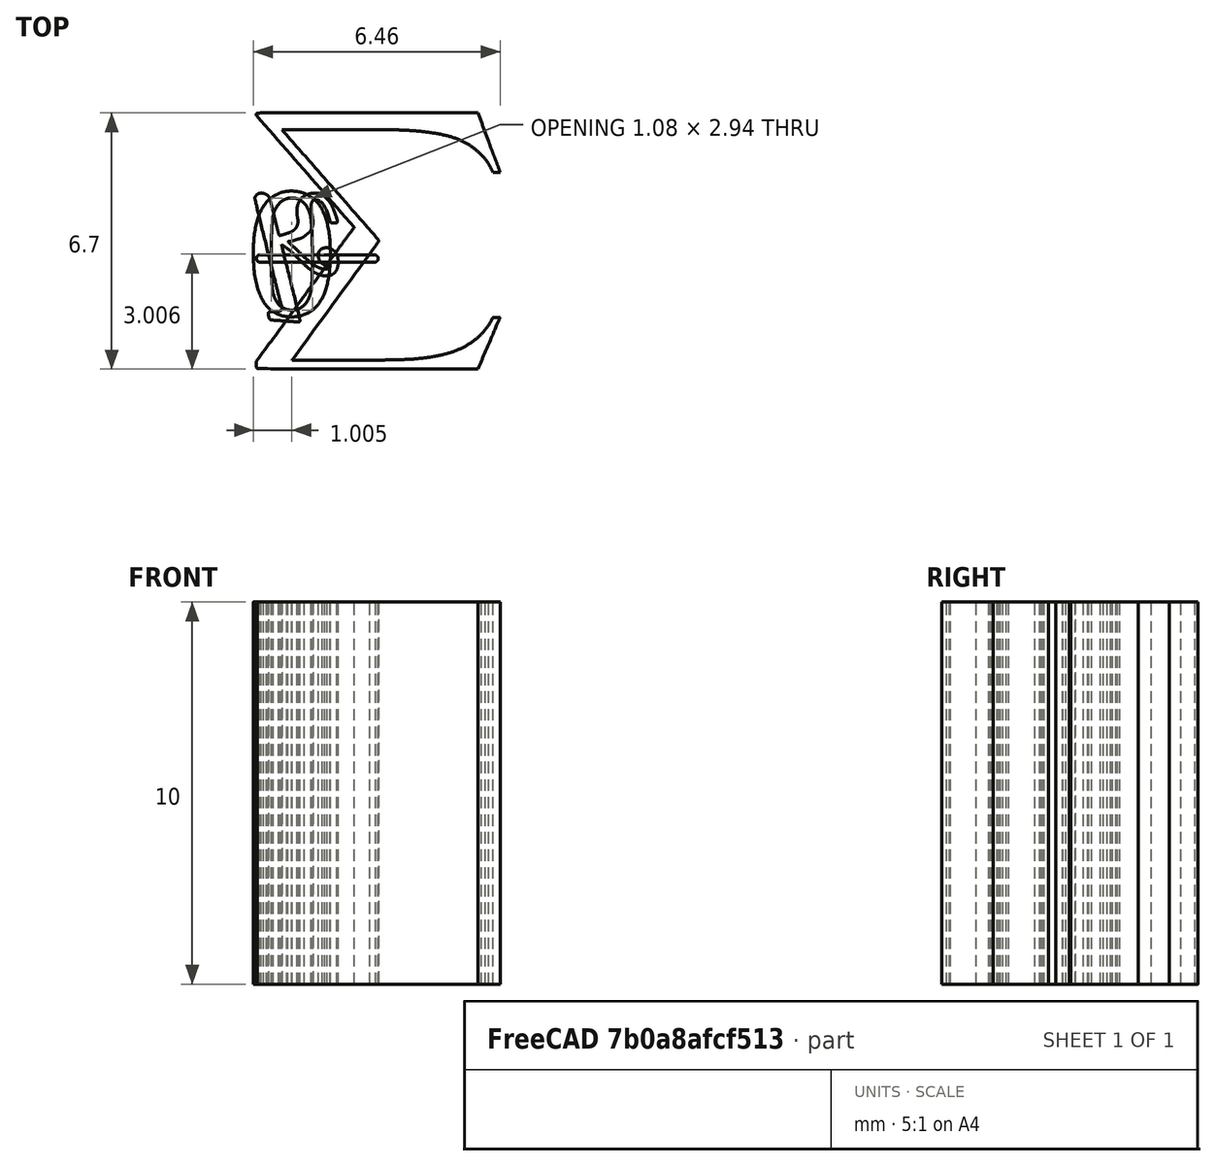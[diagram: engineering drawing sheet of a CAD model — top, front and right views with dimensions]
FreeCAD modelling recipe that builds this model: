
FCSTD DOCUMENT  (FreeCAD 0.19R)
Label: 9
License: All rights reserved
LicenseURL: http://en.wikipedia.org/wiki/All_rights_reserved
objects: Part::Feature×8, Sketcher::SketchObject×4, PartDesign::Pad×4, PartDesign::Body×4
note: 24 computed .brp shape members not serialized (recipe doc carries the construction recipe); baked Part::Feature solids carry a one-line shape summary decoded from their .brp

FEATURE [Part::Feature] MJX_11_TEX_LO_2211
  shape: bbox 6.384 x 6.704 x 2e-07 mm, 0 faces, 0 solids (baked)
FEATURE [Part::Feature] MJX_11_TEX_I_6B
  shape: bbox 2.179 x 3.376 x 2e-07 mm, 0 faces, 0 solids (baked)
FEATURE [Part::Feature] MJX_11_TEX_N_3D
  shape: bbox 3.189 x 0.1916 x 2e-07 mm, 0 faces, 0 solids (baked)
FEATURE [Part::Feature] MJX_11_TEX_N_3D001
  shape: bbox 3.189 x 0.1916 x 2e-07 mm, 0 faces, 0 solids (baked)
FEATURE [Part::Feature] MJX_11_TEX_N_30
  shape: bbox 2.016 x 3.295 x 2e-07 mm, 0 faces, 0 solids (baked)
FEATURE [Part::Feature] MJX_11_TEX_N_30001
  shape: bbox 1.077 x 2.936 x 2e-07 mm, 0 faces, 0 solids (baked)
FEATURE [Part::Feature] MJX_11_TEX_N_32
  shape: bbox 1.911 x 3.189 x 2e-07 mm, 0 faces, 0 solids (baked)
FEATURE [Part::Feature] MJX_11_TEX_N_33
  shape: bbox 1.987 x 3.29 x 2e-07 mm, 0 faces, 0 solids (baked)
FEATURE [Sketcher::SketchObject] Sketch
  FullyConstrained = false
  MapMode = 5
  Support = -> [XY_Plane]
  sketch-geometry (43):
    g0: BSplineCurve PolesCount=3 KnotsCount=2 Degree=2 IsPeriodic=0
    g1: BSplineCurve PolesCount=2 KnotsCount=2 Degree=1 IsPeriodic=0
    g2: BSplineCurve PolesCount=2 KnotsCount=2 Degree=1 IsPeriodic=0
    g3: BSplineCurve PolesCount=3 KnotsCount=2 Degree=2 IsPeriodic=0
    g4: BSplineCurve PolesCount=2 KnotsCount=2 Degree=1 IsPeriodic=0
    g5: BSplineCurve PolesCount=2 KnotsCount=2 Degree=1 IsPeriodic=0
    g6: BSplineCurve PolesCount=3 KnotsCount=2 Degree=2 IsPeriodic=0
    g7: BSplineCurve PolesCount=3 KnotsCount=2 Degree=2 IsPeriodic=0
    g8: BSplineCurve PolesCount=3 KnotsCount=2 Degree=2 IsPeriodic=0
    g9: BSplineCurve PolesCount=3 KnotsCount=2 Degree=2 IsPeriodic=0
    g10: BSplineCurve PolesCount=3 KnotsCount=2 Degree=2 IsPeriodic=0
    g11: BSplineCurve PolesCount=2 KnotsCount=2 Degree=1 IsPeriodic=0
    g12: BSplineCurve PolesCount=2 KnotsCount=2 Degree=1 IsPeriodic=0
    g13: BSplineCurve PolesCount=2 KnotsCount=2 Degree=1 IsPeriodic=0
    g14: BSplineCurve PolesCount=2 KnotsCount=2 Degree=1 IsPeriodic=0
    g15: BSplineCurve PolesCount=3 KnotsCount=2 Degree=2 IsPeriodic=0
    g16: BSplineCurve PolesCount=3 KnotsCount=2 Degree=2 IsPeriodic=0
    g17: BSplineCurve PolesCount=3 KnotsCount=2 Degree=2 IsPeriodic=0
    g18: BSplineCurve PolesCount=2 KnotsCount=2 Degree=1 IsPeriodic=0
    g19: BSplineCurve PolesCount=3 KnotsCount=2 Degree=2 IsPeriodic=0
    g20: BSplineCurve PolesCount=3 KnotsCount=2 Degree=2 IsPeriodic=0
    g21: BSplineCurve PolesCount=3 KnotsCount=2 Degree=2 IsPeriodic=0
    g22: BSplineCurve PolesCount=3 KnotsCount=2 Degree=2 IsPeriodic=0
    g23: BSplineCurve PolesCount=3 KnotsCount=2 Degree=2 IsPeriodic=0
    g24: BSplineCurve PolesCount=3 KnotsCount=2 Degree=2 IsPeriodic=0
    g25: BSplineCurve PolesCount=3 KnotsCount=2 Degree=2 IsPeriodic=0
    g26: BSplineCurve PolesCount=3 KnotsCount=2 Degree=2 IsPeriodic=0
    g27: BSplineCurve PolesCount=2 KnotsCount=2 Degree=1 IsPeriodic=0
    g28: BSplineCurve PolesCount=3 KnotsCount=2 Degree=2 IsPeriodic=0
    g29: BSplineCurve PolesCount=3 KnotsCount=2 Degree=2 IsPeriodic=0
    g30: BSplineCurve PolesCount=3 KnotsCount=2 Degree=2 IsPeriodic=0
    g31: BSplineCurve PolesCount=2 KnotsCount=2 Degree=1 IsPeriodic=0
    g32: BSplineCurve PolesCount=2 KnotsCount=2 Degree=1 IsPeriodic=0
    g33: BSplineCurve PolesCount=3 KnotsCount=2 Degree=2 IsPeriodic=0
    g34: BSplineCurve PolesCount=3 KnotsCount=2 Degree=2 IsPeriodic=0
    g35: BSplineCurve PolesCount=3 KnotsCount=2 Degree=2 IsPeriodic=0
    g36: BSplineCurve PolesCount=2 KnotsCount=2 Degree=1 IsPeriodic=0
    g37: BSplineCurve PolesCount=3 KnotsCount=2 Degree=2 IsPeriodic=0
    g38: BSplineCurve PolesCount=3 KnotsCount=2 Degree=2 IsPeriodic=0
    g39: BSplineCurve PolesCount=3 KnotsCount=2 Degree=2 IsPeriodic=0
    g40: BSplineCurve PolesCount=2 KnotsCount=2 Degree=1 IsPeriodic=0
    g41: BSplineCurve PolesCount=2 KnotsCount=2 Degree=1 IsPeriodic=0
    g42: BSplineCurve PolesCount=3 KnotsCount=2 Degree=2 IsPeriodic=0
  constraints (43):
    c: Coincident(g0,g1)
    c: Coincident(g1,g2)
    c: Coincident(g2,g3)
    c: Coincident(g3,g4)
    c: Coincident(g4,g5)
    c: Coincident(g5,g6)
    c: Coincident(g6,g7)
    c: Coincident(g7,g8)
    c: Coincident(g8,g9)
    c: Coincident(g9,g10)
    c: Coincident(g10,g11)
    c: Coincident(g11,g12)
    c: Coincident(g12,g13)
    c: Coincident(g13,g14)
    c: Coincident(g14,g15)
    c: Coincident(g15,g16)
    c: Coincident(g16,g17)
    c: Coincident(g17,g18)
    c: Coincident(g18,g19)
    c: Coincident(g19,g20)
    c: Coincident(g20,g21)
    c: Coincident(g21,g22)
    c: Coincident(g22,g23)
    c: Coincident(g23,g24)
    c: Coincident(g24,g25)
    c: Coincident(g25,g26)
    c: Coincident(g26,g27)
    c: Coincident(g27,g28)
    c: Coincident(g28,g29)
    c: Coincident(g29,g30)
    c: Coincident(g30,g31)
    c: Coincident(g31,g32)
    c: Coincident(g32,g33)
    c: Coincident(g33,g34)
    c: Coincident(g34,g35)
    c: Coincident(g35,g36)
    c: Coincident(g36,g37)
    c: Coincident(g37,g38)
    c: Coincident(g38,g39)
    c: Coincident(g39,g40)
    c: Coincident(g40,g41)
    c: Coincident(g41,g42)
    c: Coincident(g42,g0)
FEATURE [Sketcher::SketchObject] Sketch001
  FullyConstrained = false
  MapMode = 5
  Support = -> [XY_Plane003]
  sketch-geometry (70):
    g0: BSplineCurve PolesCount=3 KnotsCount=2 Degree=2 IsPeriodic=0
    g1: BSplineCurve PolesCount=3 KnotsCount=2 Degree=2 IsPeriodic=0
    g2: BSplineCurve PolesCount=3 KnotsCount=2 Degree=2 IsPeriodic=0
    g3: BSplineCurve PolesCount=3 KnotsCount=2 Degree=2 IsPeriodic=0
    g4: BSplineCurve PolesCount=3 KnotsCount=2 Degree=2 IsPeriodic=0
    g5: BSplineCurve PolesCount=3 KnotsCount=2 Degree=2 IsPeriodic=0
    g6: BSplineCurve PolesCount=3 KnotsCount=2 Degree=2 IsPeriodic=0
    g7: BSplineCurve PolesCount=3 KnotsCount=2 Degree=2 IsPeriodic=0
    g8: BSplineCurve PolesCount=3 KnotsCount=2 Degree=2 IsPeriodic=0
    g9: BSplineCurve PolesCount=3 KnotsCount=2 Degree=2 IsPeriodic=0
    g10: BSplineCurve PolesCount=3 KnotsCount=2 Degree=2 IsPeriodic=0
    g11: BSplineCurve PolesCount=3 KnotsCount=2 Degree=2 IsPeriodic=0
    g12: BSplineCurve PolesCount=3 KnotsCount=2 Degree=2 IsPeriodic=0
    g13: BSplineCurve PolesCount=3 KnotsCount=2 Degree=2 IsPeriodic=0
    g14: BSplineCurve PolesCount=3 KnotsCount=2 Degree=2 IsPeriodic=0
    g15: BSplineCurve PolesCount=3 KnotsCount=2 Degree=2 IsPeriodic=0
    g16: BSplineCurve PolesCount=3 KnotsCount=2 Degree=2 IsPeriodic=0
    g17: BSplineCurve PolesCount=3 KnotsCount=2 Degree=2 IsPeriodic=0
    g18: BSplineCurve PolesCount=3 KnotsCount=2 Degree=2 IsPeriodic=0
    g19: BSplineCurve PolesCount=3 KnotsCount=2 Degree=2 IsPeriodic=0
    g20: BSplineCurve PolesCount=3 KnotsCount=2 Degree=2 IsPeriodic=0
    g21: BSplineCurve PolesCount=2 KnotsCount=2 Degree=1 IsPeriodic=0
    g22: BSplineCurve PolesCount=3 KnotsCount=2 Degree=2 IsPeriodic=0
    g23: BSplineCurve PolesCount=2 KnotsCount=2 Degree=1 IsPeriodic=0
    g24: BSplineCurve PolesCount=3 KnotsCount=2 Degree=2 IsPeriodic=0
    g25: BSplineCurve PolesCount=3 KnotsCount=2 Degree=2 IsPeriodic=0
    g26: BSplineCurve PolesCount=3 KnotsCount=2 Degree=2 IsPeriodic=0
    g27: BSplineCurve PolesCount=3 KnotsCount=2 Degree=2 IsPeriodic=0
    g28: BSplineCurve PolesCount=3 KnotsCount=2 Degree=2 IsPeriodic=0
    g29: BSplineCurve PolesCount=3 KnotsCount=2 Degree=2 IsPeriodic=0
    g30: BSplineCurve PolesCount=3 KnotsCount=2 Degree=2 IsPeriodic=0
    g31: BSplineCurve PolesCount=3 KnotsCount=2 Degree=2 IsPeriodic=0
    g32: BSplineCurve PolesCount=3 KnotsCount=2 Degree=2 IsPeriodic=0
    g33: BSplineCurve PolesCount=3 KnotsCount=2 Degree=2 IsPeriodic=0
    g34: BSplineCurve PolesCount=3 KnotsCount=2 Degree=2 IsPeriodic=0
    g35: BSplineCurve PolesCount=3 KnotsCount=2 Degree=2 IsPeriodic=0
    g36: BSplineCurve PolesCount=3 KnotsCount=2 Degree=2 IsPeriodic=0
    g37: BSplineCurve PolesCount=3 KnotsCount=2 Degree=2 IsPeriodic=0
    g38: BSplineCurve PolesCount=3 KnotsCount=2 Degree=2 IsPeriodic=0
    g39: BSplineCurve PolesCount=2 KnotsCount=2 Degree=1 IsPeriodic=0
    g40: BSplineCurve PolesCount=3 KnotsCount=2 Degree=2 IsPeriodic=0
    g41: BSplineCurve PolesCount=3 KnotsCount=2 Degree=2 IsPeriodic=0
    g42: BSplineCurve PolesCount=3 KnotsCount=2 Degree=2 IsPeriodic=0
    g43: BSplineCurve PolesCount=3 KnotsCount=2 Degree=2 IsPeriodic=0
    g44: BSplineCurve PolesCount=3 KnotsCount=2 Degree=2 IsPeriodic=0
    g45: BSplineCurve PolesCount=3 KnotsCount=2 Degree=2 IsPeriodic=0
    g46: BSplineCurve PolesCount=3 KnotsCount=2 Degree=2 IsPeriodic=0
    g47: BSplineCurve PolesCount=3 KnotsCount=2 Degree=2 IsPeriodic=0
    g48: BSplineCurve PolesCount=3 KnotsCount=2 Degree=2 IsPeriodic=0
    g49: BSplineCurve PolesCount=3 KnotsCount=2 Degree=2 IsPeriodic=0
    g50: BSplineCurve PolesCount=3 KnotsCount=2 Degree=2 IsPeriodic=0
    g51: BSplineCurve PolesCount=2 KnotsCount=2 Degree=1 IsPeriodic=0
    g52: BSplineCurve PolesCount=3 KnotsCount=2 Degree=2 IsPeriodic=0
    g53: BSplineCurve PolesCount=3 KnotsCount=2 Degree=2 IsPeriodic=0
    g54: BSplineCurve PolesCount=3 KnotsCount=2 Degree=2 IsPeriodic=0
    g55: BSplineCurve PolesCount=3 KnotsCount=2 Degree=2 IsPeriodic=0
    g56: BSplineCurve PolesCount=3 KnotsCount=2 Degree=2 IsPeriodic=0
    g57: BSplineCurve PolesCount=3 KnotsCount=2 Degree=2 IsPeriodic=0
    g58: BSplineCurve PolesCount=3 KnotsCount=2 Degree=2 IsPeriodic=0
    g59: BSplineCurve PolesCount=3 KnotsCount=2 Degree=2 IsPeriodic=0
    g60: BSplineCurve PolesCount=3 KnotsCount=2 Degree=2 IsPeriodic=0
    g61: BSplineCurve PolesCount=3 KnotsCount=2 Degree=2 IsPeriodic=0
    g62: BSplineCurve PolesCount=3 KnotsCount=2 Degree=2 IsPeriodic=0
    g63: BSplineCurve PolesCount=2 KnotsCount=2 Degree=1 IsPeriodic=0
    g64: BSplineCurve PolesCount=3 KnotsCount=2 Degree=2 IsPeriodic=0
    g65: BSplineCurve PolesCount=3 KnotsCount=2 Degree=2 IsPeriodic=0
    g66: BSplineCurve PolesCount=2 KnotsCount=2 Degree=1 IsPeriodic=0
    g67: BSplineCurve PolesCount=3 KnotsCount=2 Degree=2 IsPeriodic=0
    g68: BSplineCurve PolesCount=3 KnotsCount=2 Degree=2 IsPeriodic=0
    g69: BSplineCurve PolesCount=3 KnotsCount=2 Degree=2 IsPeriodic=0
  constraints (70):
    c: Coincident(g0,g1)
    c: Coincident(g1,g2)
    c: Coincident(g2,g3)
    c: Coincident(g3,g4)
    c: Coincident(g4,g5)
    c: Coincident(g5,g6)
    c: Coincident(g6,g7)
    c: Coincident(g7,g8)
    c: Coincident(g8,g9)
    c: Coincident(g9,g10)
    c: Coincident(g10,g11)
    c: Coincident(g11,g12)
    c: Coincident(g12,g13)
    c: Coincident(g13,g14)
    c: Coincident(g14,g15)
    c: Coincident(g15,g16)
    c: Coincident(g16,g17)
    c: Coincident(g17,g18)
    c: Coincident(g18,g19)
    c: Coincident(g19,g20)
    c: Coincident(g20,g21)
    c: Coincident(g21,g22)
    c: Coincident(g22,g23)
    c: Coincident(g23,g24)
    c: Coincident(g24,g25)
    c: Coincident(g25,g26)
    c: Coincident(g26,g27)
    c: Coincident(g27,g28)
    c: Coincident(g28,g29)
    c: Coincident(g29,g30)
    c: Coincident(g30,g31)
    c: Coincident(g31,g32)
    c: Coincident(g32,g33)
    c: Coincident(g33,g34)
    c: Coincident(g34,g35)
    c: Coincident(g35,g36)
    c: Coincident(g36,g37)
    c: Coincident(g37,g38)
    c: Coincident(g38,g39)
    c: Coincident(g39,g40)
    c: Coincident(g40,g41)
    c: Coincident(g41,g42)
    c: Coincident(g42,g43)
    c: Coincident(g43,g44)
    c: Coincident(g44,g45)
    c: Coincident(g45,g46)
    c: Coincident(g46,g47)
    c: Coincident(g47,g48)
    c: Coincident(g48,g49)
    c: Coincident(g49,g50)
    c: Coincident(g50,g51)
    c: Coincident(g51,g52)
    c: Coincident(g52,g53)
    c: Coincident(g53,g54)
    c: Coincident(g54,g55)
    c: Coincident(g55,g56)
    c: Coincident(g56,g57)
    c: Coincident(g57,g58)
    c: Coincident(g58,g59)
    c: Coincident(g59,g60)
    c: Coincident(g60,g61)
    c: Coincident(g61,g62)
    c: Coincident(g62,g63)
    c: Coincident(g63,g64)
    c: Coincident(g64,g65)
    c: Coincident(g65,g66)
    c: Coincident(g66,g67)
    c: Coincident(g67,g68)
    c: Coincident(g68,g69)
    c: Coincident(g69,g0)
FEATURE [Sketcher::SketchObject] Sketch002
  FullyConstrained = false
  MapMode = 5
  Support = -> [XY_Plane002]
  sketch-geometry (7):
    g0: BSplineCurve PolesCount=3 KnotsCount=2 Degree=2 IsPeriodic=0
    g1: BSplineCurve PolesCount=2 KnotsCount=2 Degree=1 IsPeriodic=0
    g2: BSplineCurve PolesCount=3 KnotsCount=2 Degree=2 IsPeriodic=0
    g3: BSplineCurve PolesCount=3 KnotsCount=2 Degree=2 IsPeriodic=0
    g4: BSplineCurve PolesCount=2 KnotsCount=2 Degree=1 IsPeriodic=0
    g5: BSplineCurve PolesCount=2 KnotsCount=2 Degree=1 IsPeriodic=0
    g6: BSplineCurve PolesCount=3 KnotsCount=2 Degree=2 IsPeriodic=0
  constraints (7):
    c: Coincident(g0,g1)
    c: Coincident(g1,g2)
    c: Coincident(g2,g3)
    c: Coincident(g3,g4)
    c: Coincident(g4,g5)
    c: Coincident(g5,g6)
    c: Coincident(g6,g0)
FEATURE [Sketcher::SketchObject] Sketch003
  FullyConstrained = false
  MapMode = 5
  Support = -> [XY_Plane001]
  sketch-geometry (25):
    g0: BSplineCurve PolesCount=3 KnotsCount=2 Degree=2 IsPeriodic=0
    g1: BSplineCurve PolesCount=3 KnotsCount=2 Degree=2 IsPeriodic=0
    g2: BSplineCurve PolesCount=3 KnotsCount=2 Degree=2 IsPeriodic=0
    g3: BSplineCurve PolesCount=3 KnotsCount=2 Degree=2 IsPeriodic=0
    g4: BSplineCurve PolesCount=3 KnotsCount=2 Degree=2 IsPeriodic=0
    g5: BSplineCurve PolesCount=3 KnotsCount=2 Degree=2 IsPeriodic=0
    g6: BSplineCurve PolesCount=3 KnotsCount=2 Degree=2 IsPeriodic=0
    g7: BSplineCurve PolesCount=3 KnotsCount=2 Degree=2 IsPeriodic=0
    g8: BSplineCurve PolesCount=3 KnotsCount=2 Degree=2 IsPeriodic=0
    g9: BSplineCurve PolesCount=3 KnotsCount=2 Degree=2 IsPeriodic=0
    g10: BSplineCurve PolesCount=3 KnotsCount=2 Degree=2 IsPeriodic=0
    g11: BSplineCurve PolesCount=3 KnotsCount=2 Degree=2 IsPeriodic=0
    g12: BSplineCurve PolesCount=3 KnotsCount=2 Degree=2 IsPeriodic=0
    g13: BSplineCurve PolesCount=3 KnotsCount=2 Degree=2 IsPeriodic=0
    g14: BSplineCurve PolesCount=3 KnotsCount=2 Degree=2 IsPeriodic=0
    g15: BSplineCurve PolesCount=3 KnotsCount=2 Degree=2 IsPeriodic=0
    g16: BSplineCurve PolesCount=3 KnotsCount=2 Degree=2 IsPeriodic=0
    g17: BSplineCurve PolesCount=3 KnotsCount=2 Degree=2 IsPeriodic=0
    g18: BSplineCurve PolesCount=3 KnotsCount=2 Degree=2 IsPeriodic=0
    g19: BSplineCurve PolesCount=3 KnotsCount=2 Degree=2 IsPeriodic=0
    g20: BSplineCurve PolesCount=3 KnotsCount=2 Degree=2 IsPeriodic=0
    g21: BSplineCurve PolesCount=3 KnotsCount=2 Degree=2 IsPeriodic=0
    g22: BSplineCurve PolesCount=3 KnotsCount=2 Degree=2 IsPeriodic=0
    g23: BSplineCurve PolesCount=3 KnotsCount=2 Degree=2 IsPeriodic=0
    g24: BSplineCurve PolesCount=3 KnotsCount=2 Degree=2 IsPeriodic=0
  constraints (25):
    c: Coincident(g0,g1)
    c: Coincident(g1,g2)
    c: Coincident(g2,g3)
    c: Coincident(g3,g4)
    c: Coincident(g4,g5)
    c: Coincident(g5,g6)
    c: Coincident(g6,g7)
    c: Coincident(g7,g8)
    c: Coincident(g8,g9)
    c: Coincident(g9,g10)
    c: Coincident(g10,g11)
    c: Coincident(g11,g12)
    c: Coincident(g12,g0)
    c: Coincident(g13,g14)
    c: Coincident(g14,g15)
    c: Coincident(g15,g16)
    c: Coincident(g16,g17)
    c: Coincident(g17,g18)
    c: Coincident(g18,g19)
    c: Coincident(g19,g20)
    c: Coincident(g20,g21)
    c: Coincident(g21,g22)
    c: Coincident(g22,g23)
    c: Coincident(g23,g24)
    c: Coincident(g24,g13)
FEATURE [PartDesign::Pad] Pad
  Direction = (1,1,1)
  Length = 10
  Length2 = 100
  Profile = -> Sketch
  Type = 0
FEATURE [PartDesign::Body] Body
  Group = -> [Sketch,Pad]
  Origin = -> Origin
  Tip = -> Pad
FEATURE [PartDesign::Pad] Pad001
  Direction = (1,1,1)
  Length = 10
  Length2 = 100
  Profile = -> Sketch003
  Type = 0
FEATURE [PartDesign::Body] Body001
  Group = -> [Sketch003,Pad001]
  Origin = -> Origin001
  Tip = -> Pad001
FEATURE [PartDesign::Pad] Pad002
  Direction = (1,1,1)
  Length = 10
  Length2 = 100
  Profile = -> Sketch001
  Type = 0
FEATURE [PartDesign::Body] Body003
  Group = -> [Sketch001,Pad002]
  Origin = -> Origin003
  Tip = -> Pad002
FEATURE [PartDesign::Pad] Pad003
  Direction = (1,1,1)
  Length = 10
  Length2 = 100
  Profile = -> Sketch002
  Type = 0
FEATURE [PartDesign::Body] Body002
  Group = -> [Sketch002,Pad003]
  Origin = -> Origin002
  Tip = -> Pad003
